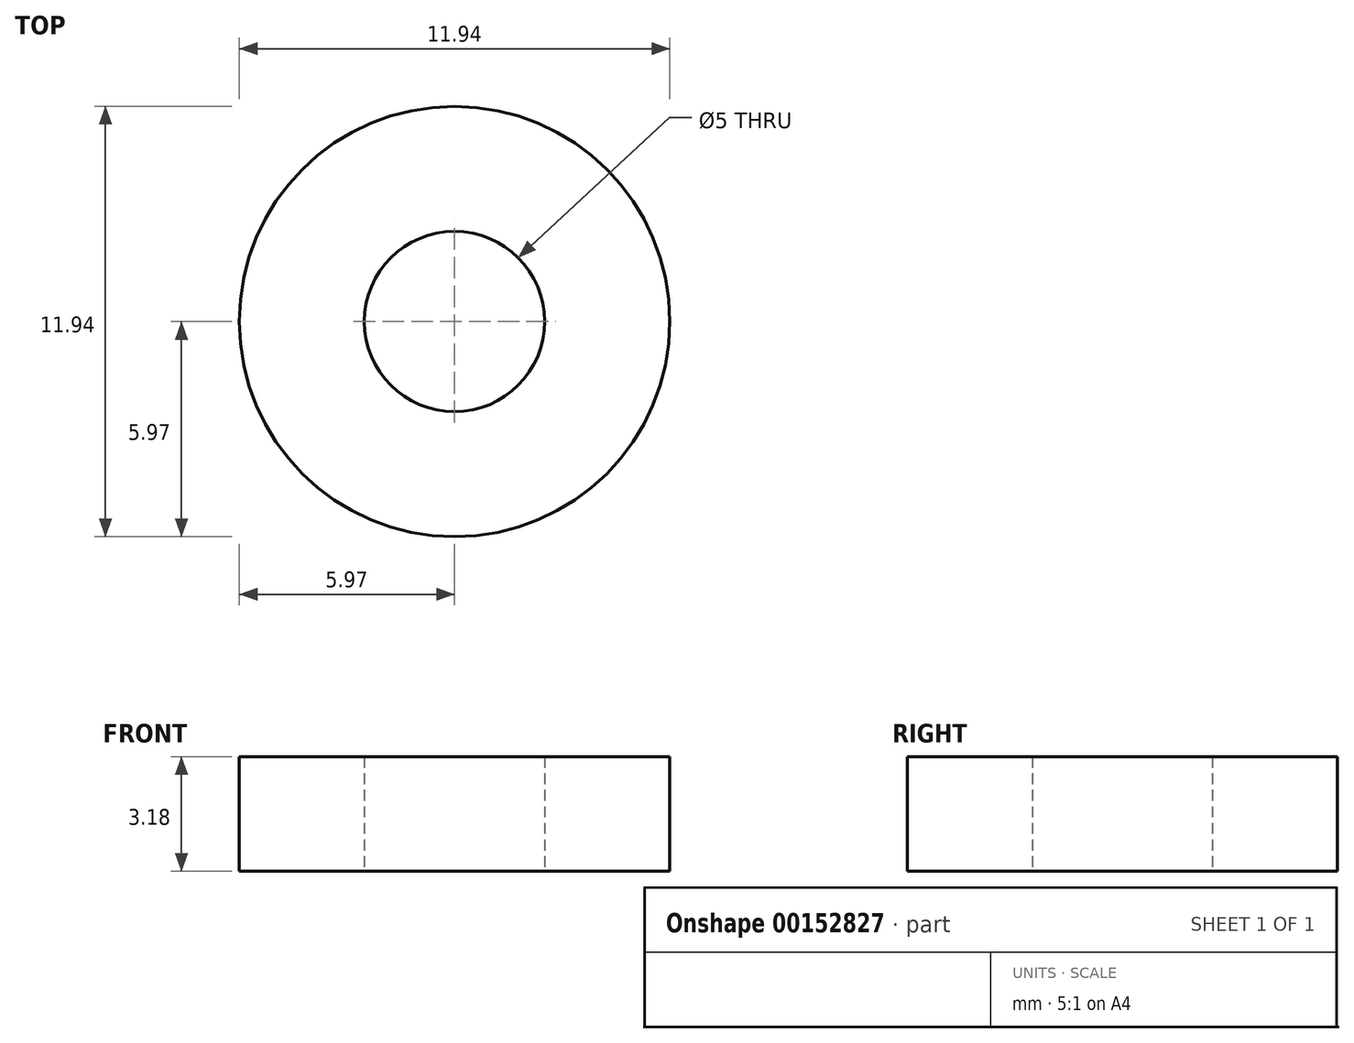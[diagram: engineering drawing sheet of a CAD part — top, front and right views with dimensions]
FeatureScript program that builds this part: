
annotation { "Feature Type Name" : "Feature", "Feature Type Description" : "" }
export const myFeature = defineFeature(function(context is Context, id is Id, definition is map)
    precondition{}
    {
        {
            var Q0;
            Q0=qCreatedBy(makeId("Top.planeOp"),FACE);
            var sketch = newSketch(context, id + "F0", { "sketchPlane" : qUnion([Q0])});
            skCircle(sketch, "E0", {"center": v(0, 0) * mm, "radius": 2.5 * mm});
            skCircle(sketch, "E1", {"center": v(0, 0) * mm, "radius": 5.97 * mm});
            skSolve(sketch);
        }
        {
            var Q0;
            Q0=qSketchRegion(id+"F0",true);
            extrude(context, id + "F1", {"entities" : qUnion([Q0]), "depth" : 3.17 * mm});
        }
    });
